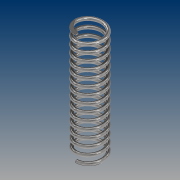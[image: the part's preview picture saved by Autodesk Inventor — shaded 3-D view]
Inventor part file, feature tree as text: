
AUTODESK INVENTOR PART (.ipt)
format: ipt  version: 2021 (Build 250183000, 183)  size: 346,624 bytes
history: native  units: mm
features: sketch x2, extrude x1, helix x1
ambient origin geometry x8: Origin, YZ Plane, XZ Plane, XY Plane, X Axis, Y Axis, Z Axis, Center Point
bodies: Solid1 (feature_tree)
feature tree (4):
  sketch  "Sketch1"  dims[d0=1.36mm d1=5.3mm d2=45.0mm d3=0.0mm]
  extrude  "Extrusion1"  Depth=5.3mm
  helix  "Coil1"  [1 undecoded]
  sketch  "Sketch2"  dims[d4=3.0mm d5=45.0mm d6=10.0mm d7=0.0mm d8=90.0deg d9=90.0deg d10=0.0mm d11=0.0mm]
note: 1 required parameter value undecoded (feature->parameter linkage not recoverable at this tier; creation-order binding heuristic only, values carry confidence <= 0.55)
